# Revit family: Desk_Accessories-Teknion-RDML_Flush_Mounted_Modesty_Panel_Solid-R2019
name_source: partatom
category: Furniture
units: mm (PartAtom-declared; Revit-internal decimal feet)

## family parameters
Always vertical = Yes
Cut with Voids When Loaded = No
OmniClass Number = 23.40.20.00
OmniClass Title = General Furniture and Specialties
Room Calculation Point = No
Shared = Yes
Work Plane-Based = No

## types (2) — shared parameters
Assembly Code = E2020200
Manufacturer = Teknion
Manufacturer Fax = 416.661.4586
Part Number = RDML
Product Documentation Link = https://www.teknion.com
Product Line = Expansion Desking
Product Page URL = https://www.teknion.com
Series = Expansion Desking
Sustainability Data = https://www.teknion.com
URL = www.teknion.com
Unit Weight URL = http://www.teknion.com
Warranty = http://www.teknion.com

## per-type parameters (varying)
| type | Bottom Modesty Panel Offset | Description | Model |
| Full-Height Modesty Panel | 0.602 " | Flush-Mounted Modesty Panel – Solid, Full-Height Modesty Panel | RDMLF__ |
| 3/4 Height Modesty Panel | 6.697 " | Flush-Mounted Modesty Panel – Solid, 3/4 Height Modesty Panel | RDMLT__ |

## geometry (parser evidence)
native form markers: Sweep x3
no freeform markers — native parametric forms only
